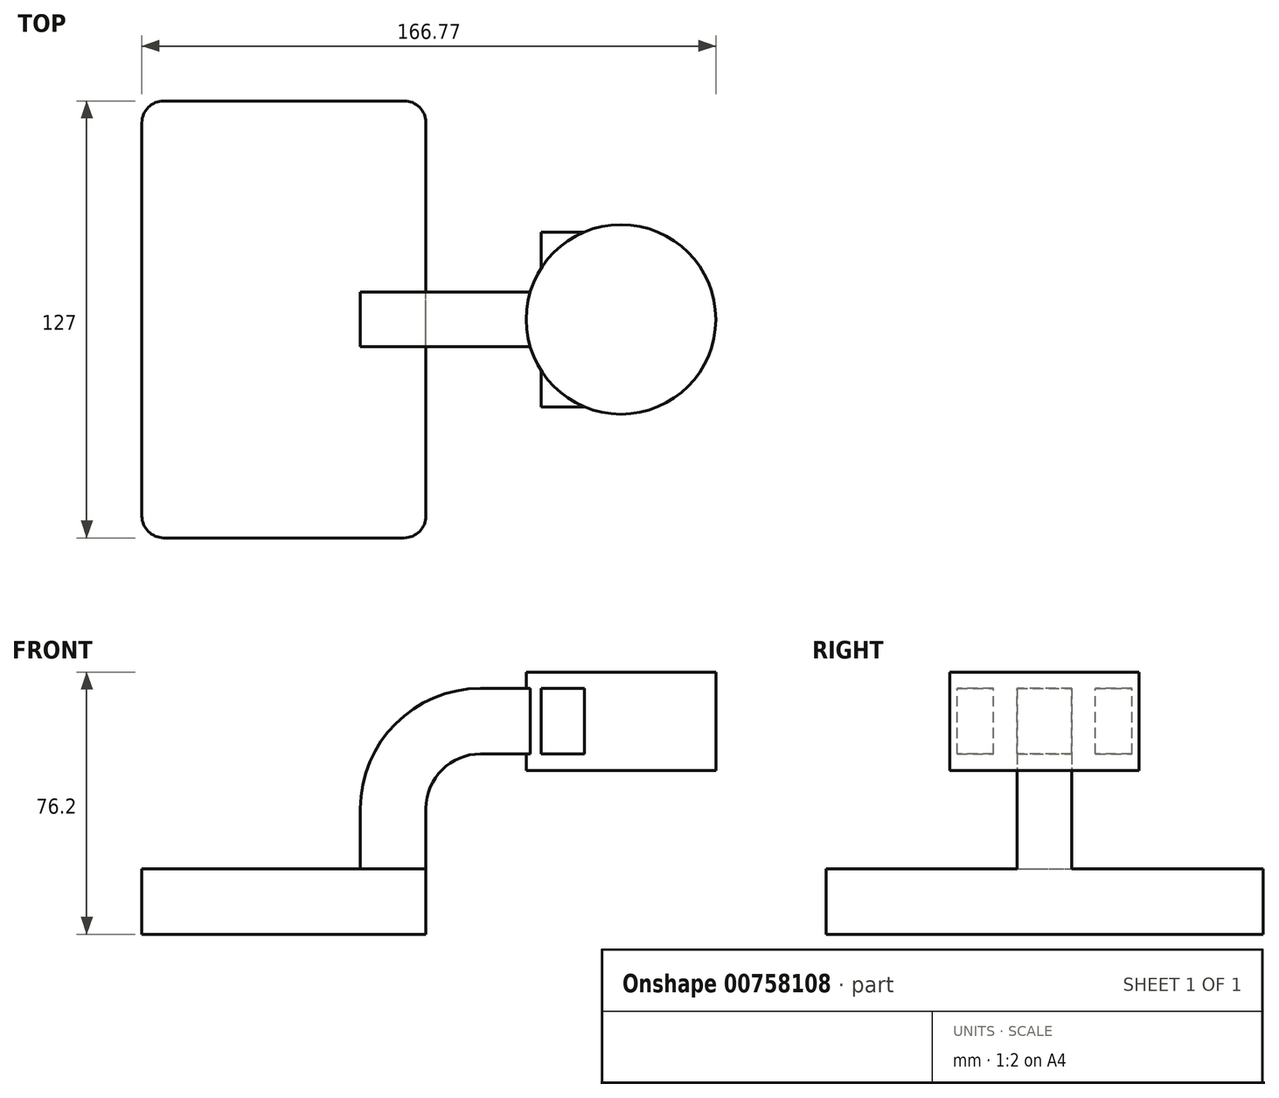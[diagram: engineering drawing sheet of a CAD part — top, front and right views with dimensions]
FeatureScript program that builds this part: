
annotation { "Feature Type Name" : "Feature", "Feature Type Description" : "" }
export const myFeature = defineFeature(function(context is Context, id is Id, definition is map)
    precondition{}
    {
        {
            var Q0;
            Q0=qCreatedBy(makeId("Front.planeOp"),FACE);
            var sketch = newSketch(context, id + "F0", { "sketchPlane" : qUnion([Q0])});
            skLineSegment(sketch, "E0.bottom", {"start": v(-28.04, 27.7) * mm, "end": v(54.51, 27.7) * mm});
            skLineSegment(sketch, "E0.top", {"start": v(-28.04, 8.64) * mm, "end": v(54.51, 8.64) * mm});
            skLineSegment(sketch, "E0.left", {"start": v(-28.04, 27.7) * mm, "end": v(-28.04, 8.64) * mm});
            skLineSegment(sketch, "E0.right", {"start": v(54.51, 27.7) * mm, "end": v(54.51, 8.64) * mm});
            skLineSegment(sketch, "E1.bottom", {"start": v(54.51, 27.7) * mm, "end": v(54.51, 27.7) * mm});
            skLineSegment(sketch, "E1.top", {"start": v(54.51, 45.17) * mm, "end": v(54.51, 45.17) * mm});
            skLineSegment(sketch, "E1.left", {"start": v(54.51, 27.7) * mm, "end": v(54.51, 45.17) * mm});
            skLineSegment(sketch, "E1.right", {"start": v(54.51, 27.7) * mm, "end": v(54.51, 45.17) * mm});
            skArc(sketch, "E2", {"start": v(54.51, 45.17) * mm, "mid": v(59.16, 56.4) * mm, "end": v(70.39, 61.04) * mm});
            skLineSegment(sketch, "E3.bottom", {"start": v(87.93, 84.84) * mm, "end": v(138.73, 84.84) * mm});
            skLineSegment(sketch, "E3.top", {"start": v(87.93, 56.27) * mm, "end": v(138.73, 56.27) * mm});
            skLineSegment(sketch, "E3.left", {"start": v(87.93, 84.84) * mm, "end": v(87.93, 56.27) * mm});
            skLineSegment(sketch, "E3.right", {"start": v(138.73, 84.84) * mm, "end": v(138.73, 56.27) * mm});
            skLineSegment(sketch, "E4", {"start": v(70.39, 61.04) * mm, "end": v(111.18, 61.04) * mm});
            skArc(sketch, "E5.0", {"start": v(35.46, 45.17) * mm, "mid": v(45.7, 69.86) * mm, "end": v(70.39, 80.1) * mm});
            skLineSegment(sketch, "E6.0", {"start": v(35.46, 27.7) * mm, "end": v(35.46, 45.17) * mm});
            skLineSegment(sketch, "E7.0", {"start": v(70.39, 80.1) * mm, "end": v(111.18, 80.1) * mm});
            skLineSegment(sketch, "E8", {"start": v(111.18, 80.1) * mm, "end": v(111.18, 61.04) * mm});
            skFitSpline(sketch, "E9", {"points": [v(-28.04, 27.7) * mm, v(70.39, 80.1) * mm], "startDerivative": vector(-0.3, 139.5) * mm, "endDerivative": vector(145.42, -24.02) * mm});
            skLineSegment(sketch, "E10", {"start": v(111.18, 80.1) * mm, "end": v(111.18, 84.84) * mm});
            skLineSegment(sketch, "E11", {"start": v(111.18, 61.04) * mm, "end": v(111.18, 56.27) * mm});
            skSolve(sketch);
        }
        {
            var Q0;
            Q0=makeQuery(id+"F0.imprint","IMPRINT",FACE,{"disambiguationData":[TD([[makeQuery(id+"F0.imprint","IMPRINT",EDGE,{"derivedFrom":sQuery(id+"F0.wireOp",EDGE,"E0.top")}),1.0]])]});
            extrude(context, id + "F1", {"entities" : qUnion([Q0]), "endBound" : BoundingType.SYMMETRIC, "depth" : 127 * mm, "offsetDistance" : 25.4 * mm});
        }
        {
            var Q0;
            {var subQ5=sQuery(id+"F0.wireOp",EDGE,"E1.right");Q0=makeQuery(id+"F0.imprint","IMPRINT",FACE,{"disambiguationData":[TD([[makeQuery(id+"F0.imprint","IMPRINT",EDGE,{"derivedFrom":subQ5}),1.0]])]});}
            var Q1;
            {var subQ5=sQuery(id+"F0.wireOp",EDGE,"E8");Q1=makeQuery(id+"F0.imprint","IMPRINT",FACE,{"disambiguationData":[TD([[makeQuery(id+"F0.imprint","IMPRINT",EDGE,{"derivedFrom":subQ5}),-1.0]])]});}
            extrude(context, id + "F2", {"entities" : qUnion([Q0, Q1]), "operationType" : NewBodyOperationType.ADD, "endBound" : BoundingType.SYMMETRIC, "depth" : 50.8 * mm, "offsetDistance" : 25.4 * mm});
        }
        {
            var Q0;
            Q0=makeQuery(id+"F0.imprint","IMPRINT",FACE,{"disambiguationData":[TD([[makeQuery(id+"F0.imprint","IMPRINT",EDGE,{"derivedFrom":sQuery(id+"F0.wireOp",EDGE,"E5.0")}),1.0]])]});
            extrude(context, id + "F3", {"entities" : qUnion([Q0]), "operationType" : NewBodyOperationType.ADD, "endBound" : BoundingType.SYMMETRIC, "depth" : 15.88 * mm, "offsetDistance" : 25.4 * mm});
        }
        {
            var Q0;
            {var subQ0=sQuery(id+"F0.wireOp",EDGE,"E3.right");Q0=makeQuery(id+"F0.imprint","IMPRINT",FACE,{"disambiguationData":[TD([[makeQuery(id+"F0.imprint","IMPRINT",EDGE,{"derivedFrom":subQ0}),-1.0]])]});}
            var Q1;
            Q1=sQuery(id+"F0.wireOp",EDGE,"E8");
            revolve(context, id + "F4", {"operationType" : NewBodyOperationType.ADD, "surfaceOperationType" : NewSurfaceOperationType.NEW, "entities" : qUnion([Q0]), "axis" : qUnion([Q1]), "revolveType" : RevolveType.FULL});
        }
        {
            var Q0;
            Q0=makeQuery(id+"F1.opExtrude","CAP_EDGE",EDGE,{"disambiguationData":[OSD([sQuery(id+"F0.wireOp",EDGE,"E0.right")])],"isStart":false});
            var Q1;
            Q1=makeQuery(id+"F1.opExtrude","CAP_EDGE",EDGE,{"disambiguationData":[OSD([sQuery(id+"F0.wireOp",EDGE,"E0.left")])],"isStart":false});
            var Q2;
            Q2=makeQuery(id+"F1.opExtrude","CAP_EDGE",EDGE,{"disambiguationData":[OSD([sQuery(id+"F0.wireOp",EDGE,"E0.left")])],"isStart":true});
            var Q3;
            Q3=makeQuery(id+"F1.opExtrude","CAP_EDGE",EDGE,{"disambiguationData":[OSD([sQuery(id+"F0.wireOp",EDGE,"E0.right")])],"isStart":true});
            fillet(context, id + "F5", {"entities" : qUnion([Q0, Q1, Q2, Q3]), "radius" : 6.35 * mm, "tangentPropagation" : true, "allowEdgeOverflow" : false});
        }
    });
